# Revit family: EL-AS1247xxWS840M9x
name_source: partatom
category: Leuchten
units: mm (PartAtom-declared; Revit-internal decimal feet)

## family parameters
Basisbauteil = Fläche
Beim Laden mit Abzugskörper schneiden = Nein
Bemaßung runder Anschluss = Durchmesser verwenden
Gemeinsam genutzt = Nein
Lichtquelle = Ja
OmniClass-Nummer = 23.80.70.11
OmniClass-Titel = Luminaries for Internal Lighting
Raumberechnungspunkt = Nein
Teiletyp = Normal

## types (4) — shared parameters
Baugruppenkennzeichen = D5020200
Emissionsform beim Rendern sichtbar = Nein
Farbfilter = 16777215
Farbtemperaturverschiebung bei Dämpfen der Lampe = <Keine Auswahl>
Hersteller = RIDI Leuchten GmbH
Lampe = LED
Neigungswinkel = 90.00°
URL = www.ridi.de
Von Breite des Rechtecks ausssenden = 1080 mm  [stored 3.54331 ft]
Von Länge des Rechtecks aussenden = 92 mm  [stored 0.301837 ft]
brand = RIDI
conformity mark = CE
electrical safety class = 1
height = 60 mm  [stored 0.19685 ft]
ingress protection (IP) code = IP20
length = 1255 mm  [stored 4.11745 ft]
nominal frequency = 50-60Hz
nominal voltage = 230
voltage type (AC, DC, UC) = AC
width = 187 mm  [stored 0.613517 ft]
zero-valued in all types: Vorgabe-Ansicht

## per-type parameters (varying)
| type | Datei für fotometrisches Netz | Modell | Scheinlast | product name | rated input power |
| EL-AS1247NDWS840M9S0550 | xxxM9Sxxx.IES | 0627906 | 38 VA | EL-AS1247NDWS840M9S0550
EL-AQ0622NDWS840M9P0400
EL-AQ0622DAWS840M9S0350 | 38 |
| EL-AS1247DAWS840M9S0550 | xxxM9Sxxx.IES | 0637906 | 38 VA | EL-AS1247DAWS840M9S0550
EL-AQ0622NDWS840M9P0400
EL-AQ0622DAWS840M9S0350 | 38 |
| EL-AS1247RFWS840M9P0600 | xxxM9Pxxx.IES | 0627910 | 37 VA | EL-AS1247RFWS840M9P0600
EL-AQ0622NDWS840M9P0400
EL-AQ0622DAWS840M9S0350 | 37 |
| EL-AS1247DAWS840M9P0600 | xxxM9Pxxx.IES | 0637910 | 37 VA | EL-AS1247DAWS840M9P0600
EL-AQ0622NDWS840M9P0400
EL-AQ0622DAWS840M9S0350 | 37 |

note: [stored X ft] marks values corroborated as IEEE doubles in the binary element streams (Revit-internal decimal feet)
